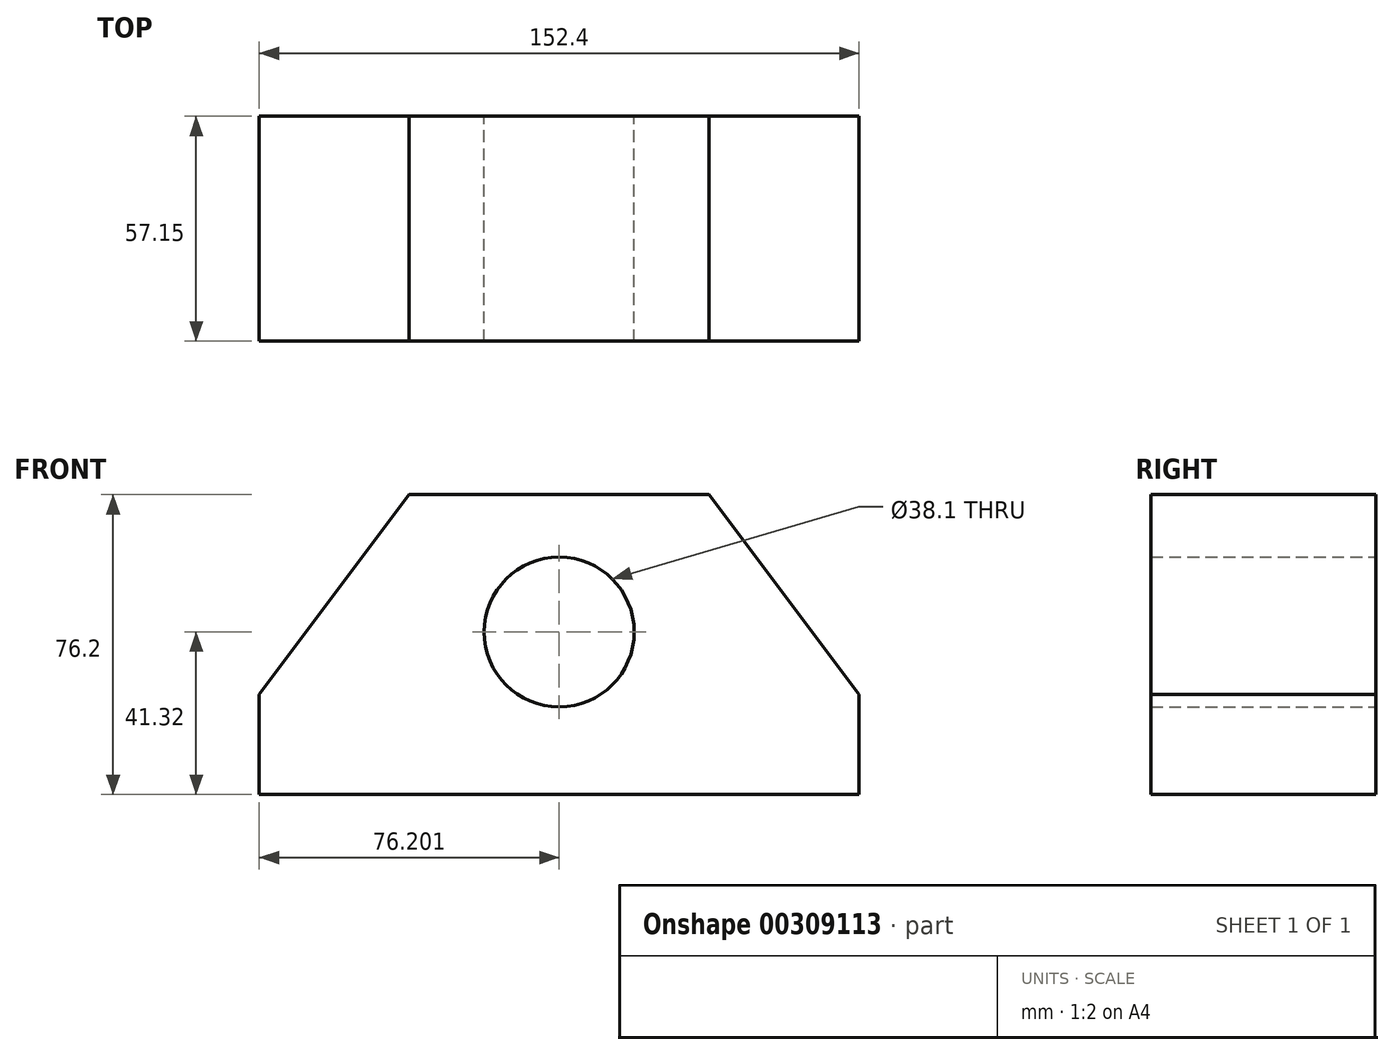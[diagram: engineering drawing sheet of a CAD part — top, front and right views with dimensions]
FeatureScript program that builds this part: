
annotation { "Feature Type Name" : "Feature", "Feature Type Description" : "" }
export const myFeature = defineFeature(function(context is Context, id is Id, definition is map)
    precondition{}
    {
        {
            var Q0;
            Q0=qCreatedBy(makeId("Front.planeOp"),FACE);
            var sketch = newSketch(context, id + "F0", { "sketchPlane" : qUnion([Q0])});
            skLineSegment(sketch, "E0", {"start": v(-58.9, -77.46) * mm, "end": v(93.5, -77.46) * mm});
            skLineSegment(sketch, "E1", {"start": v(93.5, -77.46) * mm, "end": v(93.5, -52.06) * mm});
            skLineSegment(sketch, "E2", {"start": v(-58.9, -77.46) * mm, "end": v(-58.9, -52.06) * mm});
            skLineSegment(sketch, "E3", {"start": v(-58.9, -52.06) * mm, "end": v(-20.8, -1.26) * mm});
            skLineSegment(sketch, "E4", {"start": v(93.5, -52.06) * mm, "end": v(55.4, -1.26) * mm});
            skLineSegment(sketch, "E5", {"start": v(-20.8, -1.26) * mm, "end": v(55.4, -1.26) * mm});
            skCircle(sketch, "E6", {"center": v(17.3, -36.14) * mm, "radius": 19.05 * mm});
            skSolve(sketch);
        }
        {
            var Q0;
            Q0 = qSketchRegion(id + "F0", true);
            extrude(context, id + "F1", {"entities" : qUnion([Q0]), "depth" : 57.15 * mm});
        }
    });
